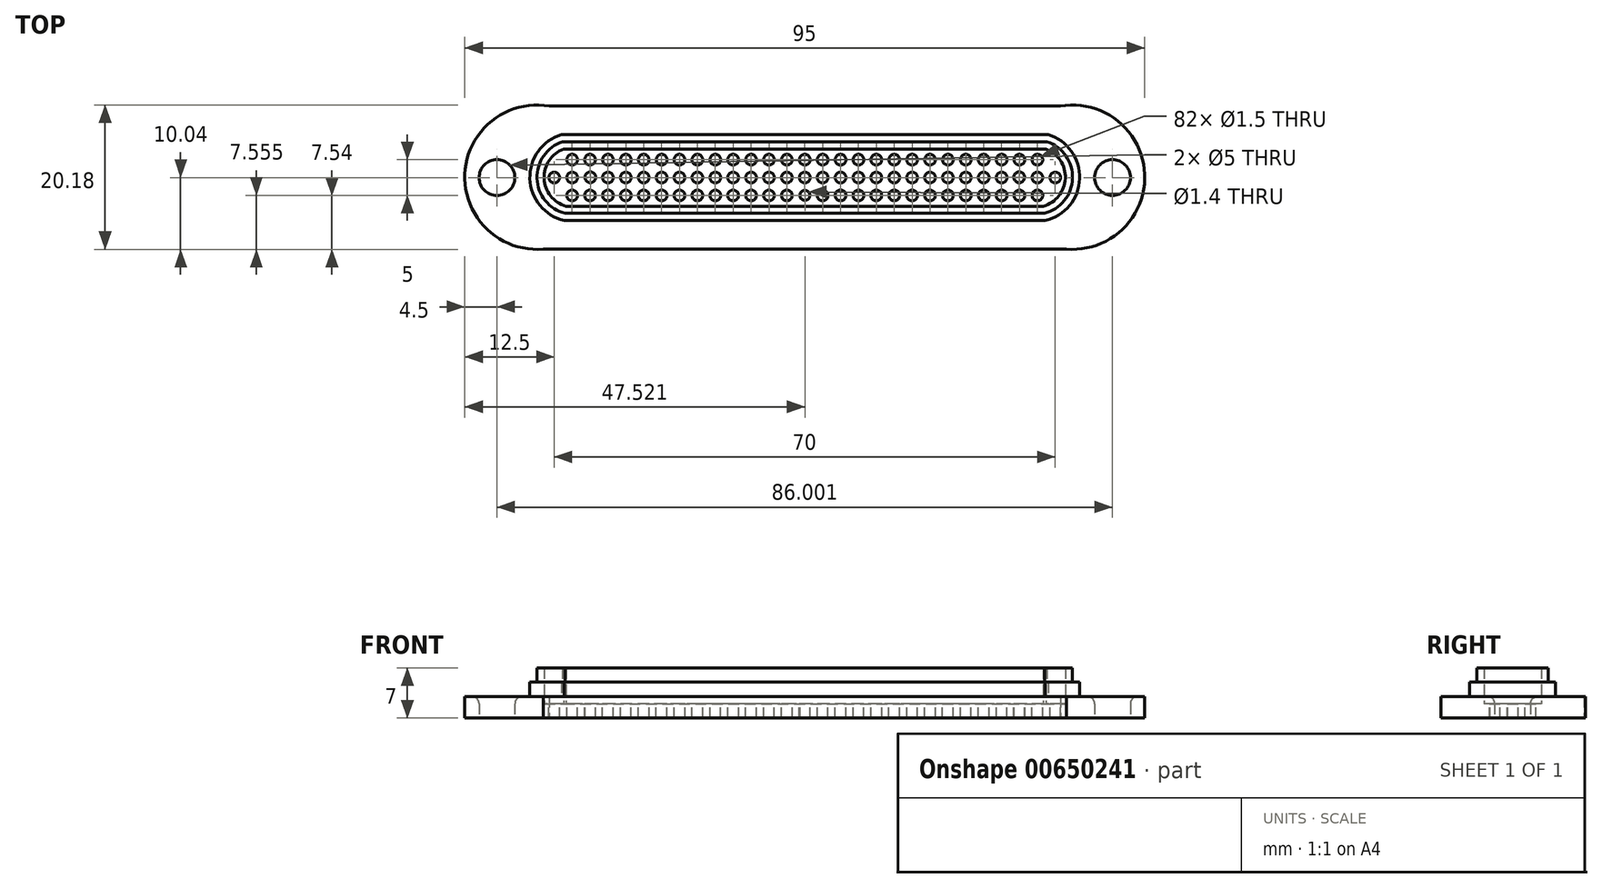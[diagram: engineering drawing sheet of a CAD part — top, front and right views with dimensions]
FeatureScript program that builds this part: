
annotation { "Feature Type Name" : "Feature", "Feature Type Description" : "" }
export const myFeature = defineFeature(function(context is Context, id is Id, definition is map)
    precondition{}
    {
        {
            var Q0;
            Q0=qCreatedBy(makeId("Top.planeOp"),FACE);
            var sketch = newSketch(context, id + "F0", { "sketchPlane" : qUnion([Q0])});
            skLineSegment(sketch, "E0.bottom", {"start": v(0, -10) * mm, "end": v(-36.54, -10) * mm});
            skLineSegment(sketch, "E0.top", {"start": v(0, 10) * mm, "end": v(-35.7, 10) * mm});
            skLineSegment(sketch, "E0.right", {"start": v(-47.5, 0) * mm, "end": v(-47.5, 0) * mm});
            skPoint(sketch, "E0.middle", {"position": v(0, 0) * mm});
            skArc(sketch, "E1", {"start": v(-35.7, 10) * mm, "mid": v(-47.5, 0.47) * mm, "end": v(-36.54, -10) * mm});
            skPoint(sketch, "E1.first.point", {"position": v(-36.54, -10) * mm});
            skPoint(sketch, "E1.second.point", {"position": v(-35.7, 10) * mm});
            skPoint(sketch, "E1.third.point", {"position": v(-47.5, 0) * mm});
            skLineSegment(sketch, "E2", {"start": v(0, 13.29) * mm, "end": v(0, -10) * mm, "construction": true});
            skPoint(sketch, "E3.orphan", {"position": v(-47.5, 10) * mm});
            skPoint(sketch, "E4.orphan", {"position": v(-47.5, -10) * mm});
            skPoint(sketch, "E0.left.end.orphan", {"position": v(47.5, 10) * mm});
            skPoint(sketch, "E0.left.start.orphan", {"position": v(47.5, -10) * mm});
            skLineSegment(sketch, "E5", {"start": v(-47.5, 0) * mm, "end": v(-43, 0) * mm, "construction": true});
            skCircle(sketch, "E6", {"center": v(-43, 0) * mm, "radius": 2.5 * mm});
            skLineSegment(sketch, "E7.0", {"start": v(0, 5) * mm, "end": v(-33.85, 5) * mm});
            skLineSegment(sketch, "E8.0", {"start": v(0, -5) * mm, "end": v(-33.48, -5) * mm});
            skArc(sketch, "E9", {"start": v(-33.85, 5) * mm, "mid": v(-37.4, -0.14) * mm, "end": v(-33.48, -5) * mm});
            skLineSegment(sketch, "E10.0", {"start": v(0, -6) * mm, "end": v(-33.6, -6) * mm});
            skArc(sketch, "E10.1", {"start": v(-34, 6) * mm, "mid": v(-38.4, -0.15) * mm, "end": v(-33.6, -6) * mm});
            skLineSegment(sketch, "E10.2", {"start": v(0, 6) * mm, "end": v(-34, 6) * mm});
            skLineSegment(sketch, "E11.0", {"start": v(0, -4) * mm, "end": v(-33.35, -4) * mm});
            skArc(sketch, "E11.1", {"start": v(-33.68, 4) * mm, "mid": v(-36.4, -0.12) * mm, "end": v(-33.35, -4) * mm});
            skLineSegment(sketch, "E11.2", {"start": v(0, 4) * mm, "end": v(-33.68, 4) * mm});
            skLineSegment(sketch, "E12.MirrorCS", {"start": v(47.5, 0) * mm, "end": v(47.5, 0) * mm});
            skLineSegment(sketch, "E13.MirrorCS", {"start": v(47.5, 0) * mm, "end": v(43, 0) * mm, "construction": true});
            skPoint(sketch, "E14.MirrorP", {"position": v(35.7, 10) * mm});
            skArc(sketch, "E15.MirrorCS", {"start": v(33.68, 4) * mm, "mid": v(36.4, -0.12) * mm, "end": v(33.35, -4) * mm});
            skArc(sketch, "E16.MirrorCS", {"start": v(35.7, 10) * mm, "mid": v(47.5, 0.47) * mm, "end": v(36.54, -10) * mm});
            skPoint(sketch, "E17.MirrorP", {"position": v(36.54, -10) * mm});
            skCircle(sketch, "E18.MirrorC", {"center": v(43, 0) * mm, "radius": 2.5 * mm});
            skArc(sketch, "E19.MirrorCS", {"start": v(34, 6) * mm, "mid": v(38.4, -0.15) * mm, "end": v(33.6, -6) * mm});
            skArc(sketch, "E20.MirrorCS", {"start": v(33.85, 5) * mm, "mid": v(37.4, -0.14) * mm, "end": v(33.48, -5) * mm});
            skPoint(sketch, "E21.MirrorP", {"position": v(47.5, 0) * mm});
            skLineSegment(sketch, "E22.MirrorCS", {"start": v(0, -6) * mm, "end": v(33.6, -6) * mm});
            skLineSegment(sketch, "E23.MirrorCS", {"start": v(0, -4) * mm, "end": v(33.35, -4) * mm});
            skLineSegment(sketch, "E24.MirrorCS", {"start": v(0, 4) * mm, "end": v(33.68, 4) * mm});
            skLineSegment(sketch, "E25.MirrorCS", {"start": v(0, 5) * mm, "end": v(33.85, 5) * mm});
            skLineSegment(sketch, "E26.MirrorCS", {"start": v(0, 6) * mm, "end": v(34, 6) * mm});
            skLineSegment(sketch, "E27.MirrorCS", {"start": v(0, -5) * mm, "end": v(33.48, -5) * mm});
            skLineSegment(sketch, "E28.MirrorCS", {"start": v(0, -10) * mm, "end": v(36.54, -10) * mm});
            skLineSegment(sketch, "E29.MirrorCS", {"start": v(0, 10) * mm, "end": v(35.7, 10) * mm});
            skSolve(sketch);
        }
        {
            var Q0;
            Q0 = qSketchRegion(id + "F0", true);
            extrude(context, id + "F1", {"entities" : qUnion([Q0]), "depth" : 3 * mm, "offsetDistance" : 25 * mm});
        }
        {
            var Q0;
            Q0=makeQuery(id+"F0.imprint","IMPRINT",FACE,{"disambiguationData":[TD([[makeQuery(id+"F0.imprint","IMPRINT",EDGE,{"derivedFrom":sQuery(id+"F0.wireOp",EDGE,"E7.0")}),-1.0]])]});
            extrude(context, id + "F2", {"entities" : qUnion([Q0]), "operationType" : NewBodyOperationType.ADD, "depth" : 5 * mm, "offsetDistance" : 25 * mm});
        }
        {
            var Q0;
            Q0=makeQuery(id+"F0.imprint","IMPRINT",FACE,{"disambiguationData":[TD([[makeQuery(id+"F0.imprint","IMPRINT",EDGE,{"derivedFrom":sQuery(id+"F0.wireOp",EDGE,"E7.0")}),1.0]])]});
            extrude(context, id + "F3", {"entities" : qUnion([Q0]), "operationType" : NewBodyOperationType.ADD, "depth" : 7 * mm, "offsetDistance" : 25 * mm});
        }
        {
            var Q0;
            Q0=makeQuery(id+"F0.imprint","IMPRINT",FACE,{"disambiguationData":[TD([[makeQuery(id+"F0.imprint","IMPRINT",EDGE,{"derivedFrom":sQuery(id+"F0.wireOp",EDGE,"E11.0")}),-1.0]])]});
            extrude(context, id + "F4", {"entities" : qUnion([Q0]), "operationType" : NewBodyOperationType.ADD, "depth" : 2 * mm, "offsetDistance" : 25 * mm});
        }
        {
            var Q0;
            Q0=makeQuery(id+"F4.opExtrude","CAP_FACE",FACE,{"disambiguationData":[OSD([sQuery(id+"F0.wireOp",EDGE,"E11.0"),sQuery(id+"F0.wireOp",EDGE,"E11.1"),sQuery(id+"F0.wireOp",EDGE,"E11.2"),sQuery(id+"F0.wireOp",EDGE,"E15.MirrorCS"),sQuery(id+"F0.wireOp",EDGE,"E23.MirrorCS"),sQuery(id+"F0.wireOp",EDGE,"E24.MirrorCS")])],"isStart":false});
            var sketch = newSketch(context, id + "F5", { "sketchPlane" : qUnion([Q0])});
            skArc(sketch, "E30", {"start": v(0, -0.75) * mm, "mid": v(0.75, 0) * mm, "end": v(0, 0.75) * mm});
            skArc(sketch, "E31.0.1.0", {"start": v(0, 1.75) * mm, "mid": v(0.75, 2.5) * mm, "end": v(0, 3.25) * mm});
            skCircle(sketch, "E31.1.0.0", {"center": v(2.5, 0) * mm, "radius": 0.75 * mm});
            skCircle(sketch, "E31.1.1.0", {"center": v(2.5, 2.5) * mm, "radius": 0.75 * mm});
            skCircle(sketch, "E31.2.0.0", {"center": v(5, 0) * mm, "radius": 0.75 * mm});
            skCircle(sketch, "E31.2.1.0", {"center": v(5, 2.5) * mm, "radius": 0.75 * mm});
            skCircle(sketch, "E31.3.0.0", {"center": v(7.5, 0) * mm, "radius": 0.75 * mm});
            skCircle(sketch, "E31.3.1.0", {"center": v(7.5, 2.5) * mm, "radius": 0.75 * mm});
            skCircle(sketch, "E31.4.0.0", {"center": v(10, 0) * mm, "radius": 0.75 * mm});
            skCircle(sketch, "E31.4.1.0", {"center": v(10, 2.5) * mm, "radius": 0.75 * mm});
            skCircle(sketch, "E31.5.0.0", {"center": v(12.5, 0) * mm, "radius": 0.75 * mm});
            skCircle(sketch, "E31.5.1.0", {"center": v(12.5, 2.5) * mm, "radius": 0.75 * mm});
            skCircle(sketch, "E31.6.0.0", {"center": v(15, 0) * mm, "radius": 0.75 * mm});
            skCircle(sketch, "E31.6.1.0", {"center": v(15, 2.5) * mm, "radius": 0.75 * mm});
            skCircle(sketch, "E31.7.0.0", {"center": v(17.5, 0) * mm, "radius": 0.75 * mm});
            skCircle(sketch, "E31.7.1.0", {"center": v(17.5, 2.5) * mm, "radius": 0.75 * mm});
            skCircle(sketch, "E31.8.0.0", {"center": v(20, 0) * mm, "radius": 0.75 * mm});
            skCircle(sketch, "E31.8.1.0", {"center": v(20, 2.5) * mm, "radius": 0.75 * mm});
            skCircle(sketch, "E31.9.0.0", {"center": v(22.5, 0) * mm, "radius": 0.75 * mm});
            skCircle(sketch, "E31.9.1.0", {"center": v(22.5, 2.5) * mm, "radius": 0.75 * mm});
            skCircle(sketch, "E31.10.0.0", {"center": v(25, 0) * mm, "radius": 0.75 * mm});
            skCircle(sketch, "E31.10.1.0", {"center": v(25, 2.5) * mm, "radius": 0.75 * mm});
            skLineSegment(sketch, "E31.direction1", {"start": v(0, 0) * mm, "end": v(2.5, 0) * mm, "construction": true});
            skLineSegment(sketch, "E31.direction2", {"start": v(0, 0) * mm, "end": v(0, 2.5) * mm, "construction": true});
            skLineSegment(sketch, "E32", {"start": v(0, 4) * mm, "end": v(0, -4) * mm, "construction": true});
            skCircle(sketch, "E33.0.1.0", {"center": v(2.5, -2.5) * mm, "radius": 0.75 * mm});
            skCircle(sketch, "E33.1.1.0", {"center": v(5, -2.5) * mm, "radius": 0.75 * mm});
            skCircle(sketch, "E33.2.1.0", {"center": v(7.5, -2.5) * mm, "radius": 0.75 * mm});
            skCircle(sketch, "E33.3.1.0", {"center": v(10, -2.5) * mm, "radius": 0.75 * mm});
            skCircle(sketch, "E33.4.1.0", {"center": v(12.5, -2.5) * mm, "radius": 0.75 * mm});
            skCircle(sketch, "E33.5.1.0", {"center": v(15, -2.5) * mm, "radius": 0.75 * mm});
            skCircle(sketch, "E33.6.1.0", {"center": v(17.5, -2.5) * mm, "radius": 0.75 * mm});
            skCircle(sketch, "E33.7.1.0", {"center": v(20, -2.5) * mm, "radius": 0.75 * mm});
            skCircle(sketch, "E33.8.1.0", {"center": v(22.5, -2.5) * mm, "radius": 0.75 * mm});
            skCircle(sketch, "E33.9.1.0", {"center": v(25, -2.5) * mm, "radius": 0.75 * mm});
            skCircle(sketch, "E33.10.0.0", {"center": v(27.5, 0) * mm, "radius": 0.75 * mm});
            skCircle(sketch, "E33.10.1.0", {"center": v(27.5, -2.5) * mm, "radius": 0.75 * mm});
            skLineSegment(sketch, "E33.direction1", {"start": v(2.5, 0) * mm, "end": v(5, 0) * mm, "construction": true});
            skLineSegment(sketch, "E33.direction2", {"start": v(2.5, 0) * mm, "end": v(2.5, -2.5) * mm, "construction": true});
            skArc(sketch, "E34.MirrorCS", {"start": v(0, 1.75) * mm, "mid": v(-0.75, 2.5) * mm, "end": v(0, 3.25) * mm});
            skCircle(sketch, "E35.MirrorC", {"center": v(-12.5, 0) * mm, "radius": 0.75 * mm});
            skCircle(sketch, "E36.MirrorC", {"center": v(-17.5, 0) * mm, "radius": 0.75 * mm});
            skCircle(sketch, "E37.MirrorC", {"center": v(-7.5, 0) * mm, "radius": 0.75 * mm});
            skCircle(sketch, "E38.MirrorC", {"center": v(-5, 0) * mm, "radius": 0.75 * mm});
            skCircle(sketch, "E39.MirrorC", {"center": v(-15, 0) * mm, "radius": 0.75 * mm});
            skCircle(sketch, "E40.MirrorC", {"center": v(-20, 0) * mm, "radius": 0.75 * mm});
            skCircle(sketch, "E41.MirrorC", {"center": v(-10, 0) * mm, "radius": 0.75 * mm});
            skCircle(sketch, "E42.MirrorC", {"center": v(-12.5, 2.5) * mm, "radius": 0.75 * mm});
            skCircle(sketch, "E43.MirrorC", {"center": v(-10, 2.5) * mm, "radius": 0.75 * mm});
            skCircle(sketch, "E44.MirrorC", {"center": v(-7.5, 2.5) * mm, "radius": 0.75 * mm});
            skCircle(sketch, "E45.MirrorC", {"center": v(-5, 2.5) * mm, "radius": 0.75 * mm});
            skCircle(sketch, "E46.MirrorC", {"center": v(-2.5, 0) * mm, "radius": 0.75 * mm});
            skCircle(sketch, "E47.MirrorC", {"center": v(-2.5, 2.5) * mm, "radius": 0.75 * mm});
            skArc(sketch, "E48.MirrorCS", {"start": v(0, -0.75) * mm, "mid": v(-0.75, 0) * mm, "end": v(0, 0.75) * mm});
            skCircle(sketch, "E49.MirrorC", {"center": v(-17.5, 2.5) * mm, "radius": 0.75 * mm});
            skCircle(sketch, "E50.MirrorC", {"center": v(-15, 2.5) * mm, "radius": 0.75 * mm});
            skLineSegment(sketch, "E51.MirrorCS", {"start": v(0, 0) * mm, "end": v(-2.5, 0) * mm, "construction": true});
            skCircle(sketch, "E52.MirrorC", {"center": v(-20, 2.5) * mm, "radius": 0.75 * mm});
            skLineSegment(sketch, "E53.MirrorCS", {"start": v(-2.5, 0) * mm, "end": v(-2.5, -2.5) * mm, "construction": true});
            skLineSegment(sketch, "E54.MirrorCS", {"start": v(-2.5, 0) * mm, "end": v(-5, 0) * mm, "construction": true});
            skCircle(sketch, "E55.MirrorC", {"center": v(-27.5, 0) * mm, "radius": 0.75 * mm});
            skCircle(sketch, "E56.MirrorC", {"center": v(-22.5, 0) * mm, "radius": 0.75 * mm});
            skCircle(sketch, "E57.MirrorC", {"center": v(-25, 0) * mm, "radius": 0.75 * mm});
            skCircle(sketch, "E58.MirrorC", {"center": v(-27.5, -2.5) * mm, "radius": 0.75 * mm});
            skCircle(sketch, "E59.MirrorC", {"center": v(-25, 2.5) * mm, "radius": 0.75 * mm});
            skCircle(sketch, "E60.MirrorC", {"center": v(-22.5, 2.5) * mm, "radius": 0.75 * mm});
            skCircle(sketch, "E61.MirrorC", {"center": v(-17.5, -2.5) * mm, "radius": 0.75 * mm});
            skCircle(sketch, "E62.MirrorC", {"center": v(-27.5, 2.5) * mm, "radius": 0.75 * mm});
            skCircle(sketch, "E63.MirrorC", {"center": v(-20, -2.5) * mm, "radius": 0.75 * mm});
            skCircle(sketch, "E64.MirrorC", {"center": v(-22.5, -2.5) * mm, "radius": 0.75 * mm});
            skCircle(sketch, "E65.MirrorC", {"center": v(-25, -2.5) * mm, "radius": 0.75 * mm});
            skCircle(sketch, "E66.MirrorC", {"center": v(-2.5, -2.5) * mm, "radius": 0.75 * mm});
            skCircle(sketch, "E67.MirrorC", {"center": v(-5, -2.5) * mm, "radius": 0.75 * mm});
            skCircle(sketch, "E68.MirrorC", {"center": v(-7.5, -2.5) * mm, "radius": 0.75 * mm});
            skCircle(sketch, "E69.MirrorC", {"center": v(-10, -2.5) * mm, "radius": 0.75 * mm});
            skCircle(sketch, "E70.MirrorC", {"center": v(-12.5, -2.5) * mm, "radius": 0.75 * mm});
            skCircle(sketch, "E71.MirrorC", {"center": v(-15, -2.5) * mm, "radius": 0.75 * mm});
            skCircle(sketch, "E72.0.1.0", {"center": v(0.02, -2.49) * mm, "radius": 0.7 * mm});
            skLineSegment(sketch, "E73", {"start": v(-27.5, 0) * mm, "end": v(-30, 0) * mm, "construction": true});
            skCircle(sketch, "E74.MirrorC", {"center": v(-29.96, 0.04) * mm, "radius": 0.75 * mm});
            skCircle(sketch, "E75.MirrorC", {"center": v(29.96, 0.04) * mm, "radius": 0.75 * mm});
            skCircle(sketch, "E76.0.11.1", {"center": v(30, -2.5) * mm, "radius": 0.75 * mm});
            skCircle(sketch, "E77.0.12.0", {"center": v(32.5, 0) * mm, "radius": 0.75 * mm});
            skCircle(sketch, "E77.0.12.1", {"center": v(32.5, -2.5) * mm, "radius": 0.75 * mm});
            skCircle(sketch, "E78.0.13.0", {"center": v(35, 0) * mm, "radius": 0.75 * mm});
            skCircle(sketch, "E79.MirrorC", {"center": v(27.5, 2.5) * mm, "radius": 0.75 * mm});
            skCircle(sketch, "E80.MirrorC", {"center": v(30, 2.5) * mm, "radius": 0.75 * mm});
            skCircle(sketch, "E81.MirrorC", {"center": v(32.5, 2.5) * mm, "radius": 0.75 * mm});
            skCircle(sketch, "E82.MirrorC", {"center": v(-30, 2.5) * mm, "radius": 0.75 * mm});
            skCircle(sketch, "E83.MirrorC", {"center": v(-32.5, 0) * mm, "radius": 0.75 * mm});
            skCircle(sketch, "E84.MirrorC", {"center": v(-30, -2.5) * mm, "radius": 0.75 * mm});
            skCircle(sketch, "E85.MirrorC", {"center": v(-32.5, -2.5) * mm, "radius": 0.75 * mm});
            skCircle(sketch, "E86.MirrorC", {"center": v(-32.5, 2.5) * mm, "radius": 0.75 * mm});
            skCircle(sketch, "E87.MirrorC", {"center": v(-35, 0) * mm, "radius": 0.75 * mm});
            skSolve(sketch);
        }
        {
            var Q0;
            Q0=qSketchRegion(id+"F5",true);
            extrude(context, id + "F6", {"entities" : qUnion([Q0]), "operationType" : NewBodyOperationType.REMOVE, "oppositeDirection" : true, "depth" : 25 * mm, "offsetDistance" : 25 * mm});
        }
        {
            var Q0;
            Q0=makeQuery(id+"F1.opExtrude","CAP_EDGE",EDGE,{"disambiguationData":[OSD([sQuery(id+"F0.wireOp",EDGE,"E6")])],"isStart":false});
            var Q1;
            Q1=makeQuery(id+"F1.opExtrude","CAP_EDGE",EDGE,{"disambiguationData":[OSD([sQuery(id+"F0.wireOp",EDGE,"E18.MirrorC")])],"isStart":false});
            fillet(context, id + "F7", {"entities" : qUnion([Q0, Q1]), "radius" : 1 * mm, "tangentPropagation" : true, "allowEdgeOverflow" : false});
        }
    });
